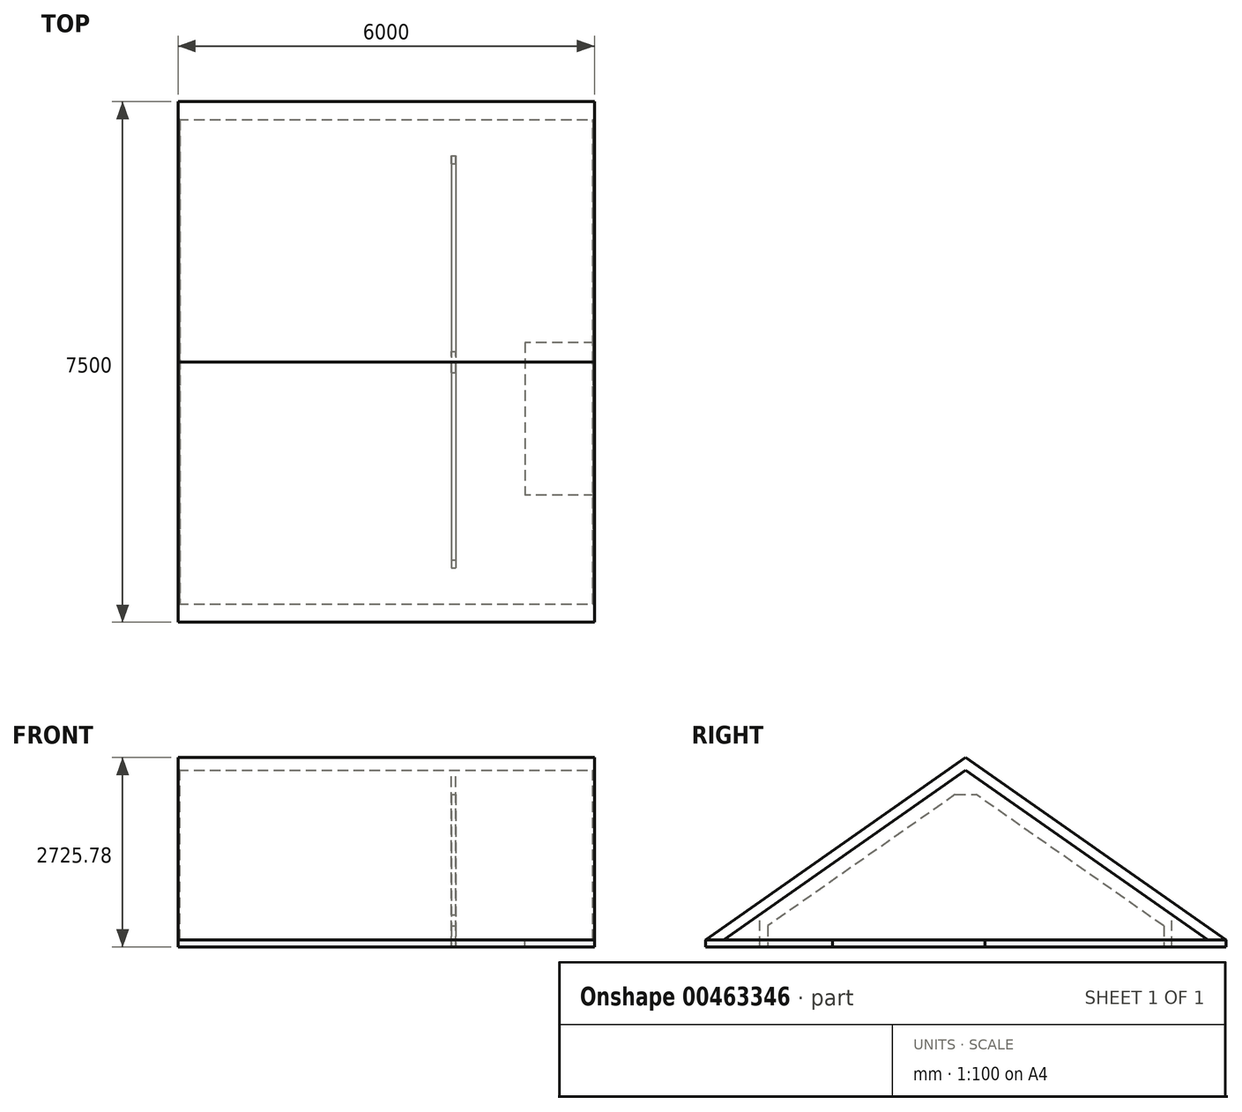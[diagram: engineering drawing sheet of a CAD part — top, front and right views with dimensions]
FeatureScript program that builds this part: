
annotation { "Feature Type Name" : "Feature", "Feature Type Description" : "" }
export const myFeature = defineFeature(function(context is Context, id is Id, definition is map)
    precondition{}
    {
        {
            var Q0;
            Q0=qCreatedBy(makeId("Top.planeOp"),FACE);
            var sketch = newSketch(context, id + "F0", { "sketchPlane" : qUnion([Q0])});
            skLineSegment(sketch, "E0.bottom", {"start": v(-3000, 3750) * mm, "end": v(3000, 3750) * mm});
            skLineSegment(sketch, "E0.top", {"start": v(-3000, -3750) * mm, "end": v(3000, -3750) * mm});
            skLineSegment(sketch, "E0.left", {"start": v(-3000, 3750) * mm, "end": v(-3000, -3750) * mm});
            skLineSegment(sketch, "E0.right", {"start": v(3000, 3750) * mm, "end": v(3000, -3750) * mm});
            skPoint(sketch, "E0.middle", {"position": v(0, 0) * mm});
            skSolve(sketch);
        }
        {
            var Q0;
            Q0 = qSketchRegion(id + "F0", true);
            extrude(context, id + "F1", {"entities" : qUnion([Q0]), "depth" : 100 * mm, "offsetDistance" : 25 * mm});
        }
        {
            var Q0;
            Q0=makeQuery(id+"F1.opExtrude","CAP_FACE",FACE,{"disambiguationData":[OSD([sQuery(id+"F0.wireOp",EDGE,"E0.bottom"),sQuery(id+"F0.wireOp",EDGE,"E0.top"),sQuery(id+"F0.wireOp",EDGE,"E0.left"),sQuery(id+"F0.wireOp",EDGE,"E0.right")])],"isStart":false});
            var sketch = newSketch(context, id + "F2", { "sketchPlane" : qUnion([Q0])});
            skLineSegment(sketch, "E1.bottom", {"start": v(3000, 280) * mm, "end": v(2000, 280) * mm});
            skLineSegment(sketch, "E1.top", {"start": v(3000, -1920) * mm, "end": v(2000, -1920) * mm});
            skLineSegment(sketch, "E1.left", {"start": v(3000, 280) * mm, "end": v(3000, -1920) * mm});
            skLineSegment(sketch, "E1.right", {"start": v(2000, 280) * mm, "end": v(2000, -1920) * mm});
            skSolve(sketch);
        }
        {
            var Q0;
            Q0=makeQuery(id+"F2.imprint","IMPRINT",FACE,{"disambiguationData":[TD([[makeQuery(id+"F2.imprint","IMPRINT",EDGE,{"derivedFrom":sQuery(id+"F2.wireOp",EDGE,"E1.bottom")}),1.0]])]});
            extrude(context, id + "F3", {"entities" : qUnion([Q0]), "operationType" : NewBodyOperationType.REMOVE, "endBound" : BoundingType.THROUGH_ALL, "oppositeDirection" : true, "depth" : 25 * mm, "offsetDistance" : 25 * mm});
        }
        {
            var Q0;
            {var subQ0=sQuery(id+"F0.wireOp",EDGE,"E0.right");var subQ2=sQuery(id+"F0.wireOp",EDGE,"E0.top");Q0=makeQuery(id+"F3.boolean.opBoolean","SPLIT",FACE,{"disambiguationData":[TD([makeQuery(id+"F1.opExtrude","SWEPT_FACE",FACE,{"disambiguationData":[OSD([subQ2])]})])],"derivedFrom":makeQuery(id+"F1.opExtrude","SWEPT_FACE",FACE,{"disambiguationData":[OSD([subQ0])]})});}
            var sketch = newSketch(context, id + "F4", { "sketchPlane" : qUnion([Q0])});
            skLineSegment(sketch, "E2", {"start": v(-3750, 100) * mm, "end": v(0, 2725.78) * mm});
            skLineSegment(sketch, "E3", {"start": v(0, 2725.78) * mm, "end": v(3750, 100) * mm});
            skLineSegment(sketch, "E4", {"start": v(-3750, 100) * mm, "end": v(-3488.48, 100) * mm});
            skLineSegment(sketch, "E5", {"start": v(-3488.48, 100) * mm, "end": v(0, 2542.66) * mm});
            skLineSegment(sketch, "E6", {"start": v(0, 2542.66) * mm, "end": v(3488.48, 100) * mm});
            skLineSegment(sketch, "E7", {"start": v(3488.48, 100) * mm, "end": v(3750, 100) * mm});
            skSolve(sketch);
        }
        {
            var Q0;
            Q0 = qSketchRegion(id + "F4", true);
            extrude(context, id + "F5", {"entities" : qUnion([Q0]), "oppositeDirection" : true, "depth" : 6000 * mm, "offsetDistance" : 25 * mm});
        }
        {
            var Q0;
            Q0=makeQuery(id+"F1.opExtrude","SWEPT_FACE",FACE,{"disambiguationData":[OSD([sQuery(id+"F0.wireOp",EDGE,"E0.left")])]});
            var sketch = newSketch(context, id + "F6", { "sketchPlane" : qUnion([Q0])});
            skLineSegment(sketch, "E8", {"start": v(-3488.48, 100) * mm, "end": v(3488.48, 100) * mm});
            skLineSegment(sketch, "E9", {"start": v(3488.48, 100) * mm, "end": v(0, 2542.66) * mm});
            skLineSegment(sketch, "E10", {"start": v(0, 2542.66) * mm, "end": v(-3488.48, 100) * mm});
            skSolve(sketch);
        }
        {
            var Q0;
            Q0=makeQuery(id+"F6.imprint","IMPRINT",FACE,{"disambiguationData":[TD([[makeQuery(id+"F6.imprint","IMPRINT",EDGE,{"derivedFrom":sQuery(id+"F6.wireOp",EDGE,"E8")}),1.0]])]});
            extrude(context, id + "F7", {"entities" : qUnion([Q0]), "oppositeDirection" : true, "depth" : 25 * mm, "offsetDistance" : 25 * mm});
        }
        {
            var Q0;
            Q0=makeQuery(id+"F7.opExtrude","SWEPT_BODY",BODY,{"disambiguationData":[OSD([sQuery(id+"F6.wireOp",EDGE,"E8"),sQuery(id+"F6.wireOp",EDGE,"E9"),sQuery(id+"F6.wireOp",EDGE,"E10")])]});
            var Q1;
            Q1=qCreatedBy(makeId("Right.planeOp"),FACE);
            mirror(context, id + "F8", {"entities" : qUnion([Q0]), "mirrorPlane" : qUnion([Q1])});
        }
        {
            var Q0;
            Q0=qCreatedBy(makeId("Right.planeOp"),FACE);
            cPlane(context, id + "F9", {"entities" : qUnion([Q0]), "cplaneType" : CPlaneType.OFFSET, "offset" : 1000 * mm, "width" : 150 * mm, "height" : 150 * mm});
        }
        {
            var Q0;
            Q0=qCreatedBy(id+"F9.planeOp",FACE);
            var sketch = newSketch(context, id + "F10", { "sketchPlane" : qUnion([Q0])});
            skLineSegment(sketch, "E11.0", {"start": v(-151.16, 2192.66) * mm, "end": v(-2854.16, 300) * mm});
            skLineSegment(sketch, "E11.1", {"start": v(2854.16, 300) * mm, "end": v(151.16, 2192.66) * mm});
            skLineSegment(sketch, "E12.0", {"start": v(0, 2542.66) * mm, "end": v(-2968.88, 463.83) * mm});
            skLineSegment(sketch, "E12.1", {"start": v(2968.88, 463.83) * mm, "end": v(0, 2542.66) * mm});
            skLineSegment(sketch, "E13", {"start": v(-2854.16, 300) * mm, "end": v(-2854.16, 0) * mm});
            skLineSegment(sketch, "E14", {"start": v(-2854.16, 0) * mm, "end": v(-2968.88, 0) * mm});
            skLineSegment(sketch, "E15", {"start": v(-2968.88, 0) * mm, "end": v(-2968.88, 463.83) * mm});
            skLineSegment(sketch, "E16", {"start": v(2854.16, 300) * mm, "end": v(2854.16, 0) * mm});
            skLineSegment(sketch, "E17", {"start": v(2854.16, 0) * mm, "end": v(2968.88, 0) * mm});
            skLineSegment(sketch, "E18", {"start": v(2968.88, 0) * mm, "end": v(2968.88, 463.83) * mm});
            skLineSegment(sketch, "E19", {"start": v(-151.16, 2192.66) * mm, "end": v(151.16, 2192.66) * mm});
            skSolve(sketch);
        }
        {
            var Q0;
            Q0=makeQuery(id+"F10.imprint","IMPRINT",FACE,{"disambiguationData":[TD([[makeQuery(id+"F10.imprint","IMPRINT",EDGE,{"derivedFrom":sQuery(id+"F10.wireOp",EDGE,"E11.0")}),-1.0]])]});
            extrude(context, id + "F11", {"entities" : qUnion([Q0]), "oppositeDirection" : true, "depth" : 60 * mm, "offsetDistance" : 25 * mm});
        }
    });
